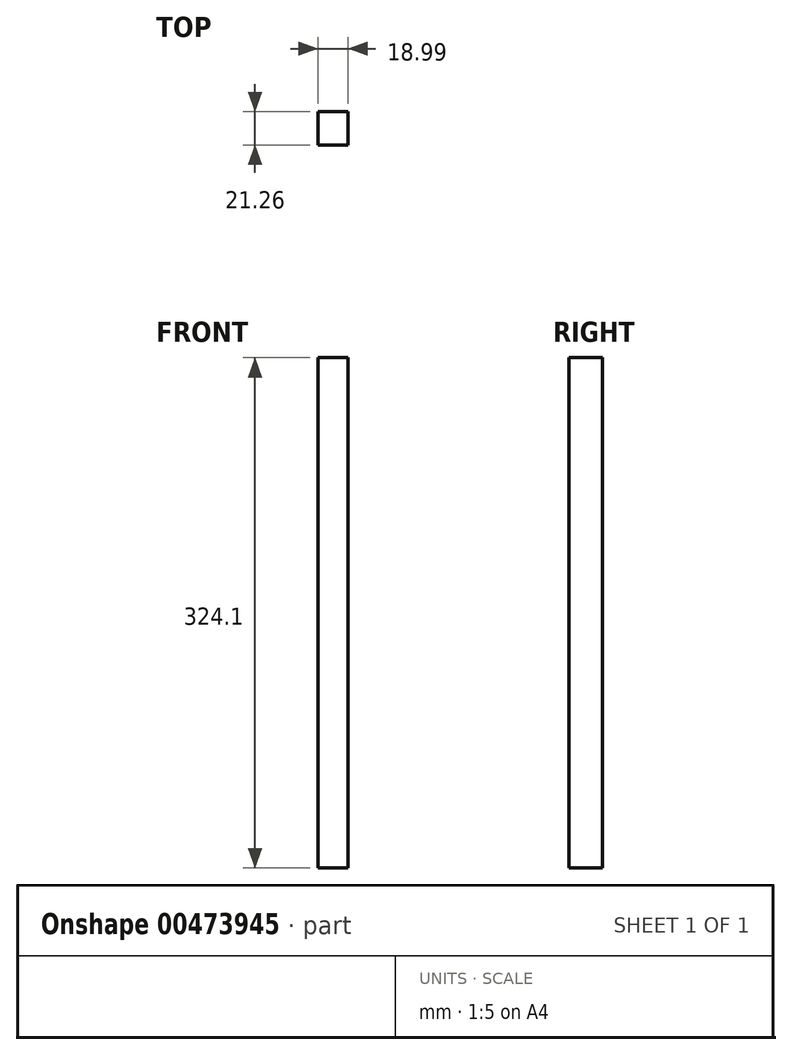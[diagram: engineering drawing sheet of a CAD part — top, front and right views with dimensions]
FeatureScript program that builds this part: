
annotation { "Feature Type Name" : "Feature", "Feature Type Description" : "" }
export const myFeature = defineFeature(function(context is Context, id is Id, definition is map)
    precondition{}
    {
        {
            var Q0;
            Q0=qCreatedBy(makeId("Top.planeOp"),FACE);
            var sketch = newSketch(context, id + "F0", { "sketchPlane" : qUnion([Q0])});
            skLineSegment(sketch, "E0.bottom", {"start": v(-119.98, 31.43) * mm, "end": v(-82, 31.43) * mm});
            skLineSegment(sketch, "E0.top", {"start": v(-119.98, -11.8) * mm, "end": v(-82, -11.8) * mm});
            skLineSegment(sketch, "E0.left", {"start": v(-119.98, 31.43) * mm, "end": v(-119.98, -11.8) * mm});
            skLineSegment(sketch, "E0.right", {"start": v(-82, 31.43) * mm, "end": v(-82, -11.8) * mm});
            skPoint(sketch, "E1.firstSnap0", {"position": v(-100.99, -11.8) * mm});
            skLineSegment(sketch, "E1.bottom", {"start": v(-100.99, 9.46) * mm, "end": v(-148.74, 9.46) * mm});
            skLineSegment(sketch, "E1.top", {"start": v(-100.99, -33.34) * mm, "end": v(-148.74, -33.34) * mm});
            skLineSegment(sketch, "E1.left", {"start": v(-100.99, 9.46) * mm, "end": v(-100.99, -33.34) * mm});
            skLineSegment(sketch, "E1.right", {"start": v(-148.74, 9.46) * mm, "end": v(-148.74, -33.34) * mm});
            skSolve(sketch);
        }
        {
            var Q0;
            {var subQ0=sQuery(id+"F0.wireOp",EDGE,"E0.left");var subQ1=sQuery(id+"F0.wireOp",EDGE,"E0.top");var subQ2=makeQuery(id+"F0.imprint","INTERSECT",VERTEX,{"derivedFrom":[subQ1,subQ0]});Q0=makeQuery(id+"F0.imprint","IMPRINT",FACE,{"disambiguationData":[TD([[makeQuery(id+"F0.imprint","IMPRINT",EDGE,{"disambiguationData":[TD([[subQ2,-1.0]])],"derivedFrom":subQ1}),1.0]])]});}
            extrude(context, id + "F1", {"entities" : qUnion([Q0]), "oppositeDirection" : true, "depth" : 324.1 * mm});
        }
    });
